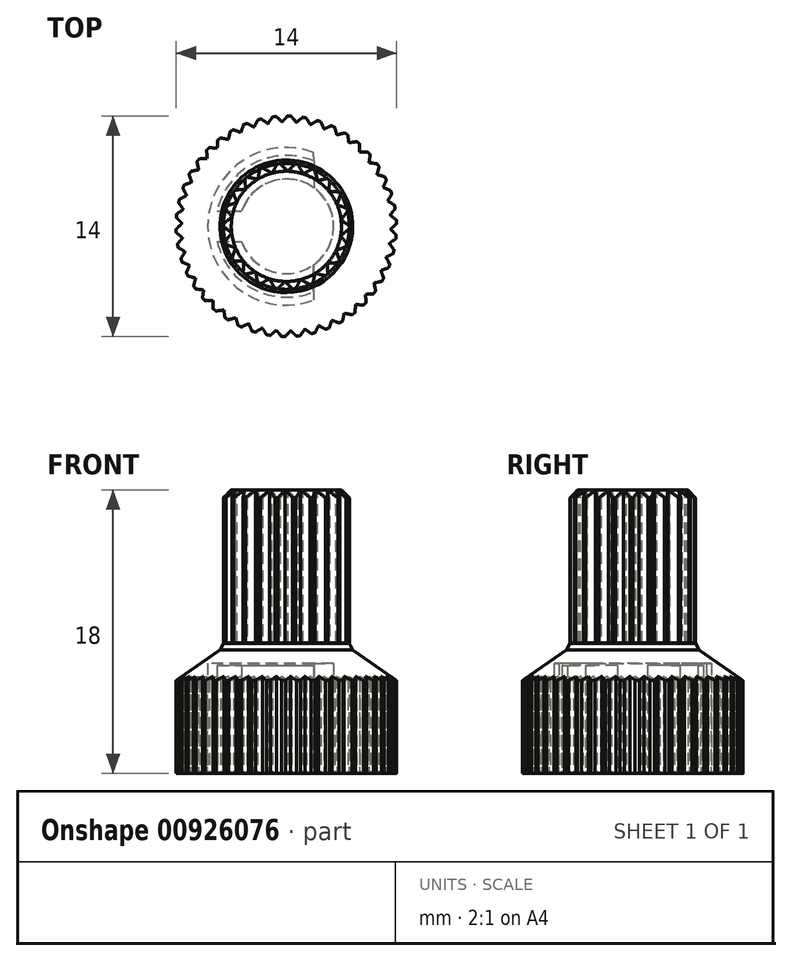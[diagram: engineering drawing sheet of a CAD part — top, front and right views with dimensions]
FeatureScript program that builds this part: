
annotation { "Feature Type Name" : "Feature", "Feature Type Description" : "" }
export const myFeature = defineFeature(function(context is Context, id is Id, definition is map)
    precondition{}
    {
        {
            var Q0;
            Q0=qCreatedBy(makeId("Top.planeOp"),FACE);
            var sketch = newSketch(context, id + "F0", { "sketchPlane" : qUnion([Q0])});
            skLineSegment(sketch, "E0", {"start": v(-2.85, 4.76) * mm, "end": v(-4.4, 4.76) * mm});
            skArc(sketch, "E1", {"start": v(-2.84, 2.85) * mm, "mid": v(3, 3.85) * mm, "end": v(-2.85, 4.76) * mm});
            skCircle(sketch, "E2", {"center": v(0, 3.83) * mm, "radius": 7 * mm});
            skArc(sketch, "E3", {"start": v(1.74, 8.52) * mm, "mid": v(-5, 3.83) * mm, "end": v(1.74, -0.86) * mm});
            skArc(sketch, "E4", {"start": v(1.76, 7.97) * mm, "mid": v(-2.08, 7.82) * mm, "end": v(-4.4, 4.76) * mm});
            skLineSegment(sketch, "E5", {"start": v(1.76, 7.97) * mm, "end": v(1.74, 8.52) * mm});
            skLineSegment(sketch, "E6", {"start": v(1.74, -0.32) * mm, "end": v(1.74, -0.86) * mm});
            skArc(sketch, "E7.trimOffspring", {"start": v(-4.4, 2.85) * mm, "mid": v(-2.07, -0.17) * mm, "end": v(1.74, -0.32) * mm});
            skLineSegment(sketch, "E8.trimOffspring", {"start": v(-4.4, 2.85) * mm, "end": v(-2.84, 2.85) * mm});
            skLineSegment(sketch, "E9", {"start": v(1.74, -0.32) * mm, "end": v(1.74, 1.38) * mm});
            skLineSegment(sketch, "E10", {"start": v(1.76, 7.97) * mm, "end": v(1.76, 6.26) * mm});
            skSolve(sketch);
        }
        {
            var Q0;
            Q0=makeQuery(id+"F0.imprint","IMPRINT",FACE,{"disambiguationData":[TD([[makeQuery(id+"F0.imprint","IMPRINT",EDGE,{"derivedFrom":sQuery(id+"F0.wireOp",EDGE,"E2")}),1.0]])]});
            var Q1;
            {var subQ0=sQuery(id+"F0.wireOp",EDGE,"E0");Q1=makeQuery(id+"F0.imprint","IMPRINT",FACE,{"disambiguationData":[TD([[makeQuery(id+"F0.imprint","IMPRINT",EDGE,{"derivedFrom":subQ0}),-1.0]])]});}
            var Q2;
            Q2=makeQuery(id+"F0.imprint","IMPRINT",FACE,{"disambiguationData":[TD([[makeQuery(id+"F0.imprint","IMPRINT",EDGE,{"derivedFrom":sQuery(id+"F0.wireOp",EDGE,"E7.trimOffspring")}),1.0]])]});
            var Q3;
            {var subQ1=sQuery(id+"F0.wireOp",EDGE,"E0");Q3=makeQuery(id+"F0.imprint","IMPRINT",FACE,{"disambiguationData":[TD([[makeQuery(id+"F0.imprint","IMPRINT",EDGE,{"derivedFrom":subQ1}),1.0]])]});}
            extrude(context, id + "F1", {"entities" : qUnion([Q0, Q1, Q2, Q3]), "depth" : 8 * mm});
        }
        {
            var Q0;
            Q0=makeQuery(id+"F0.imprint","IMPRINT",FACE,{"disambiguationData":[TD([[makeQuery(id+"F0.imprint","IMPRINT",EDGE,{"derivedFrom":sQuery(id+"F0.wireOp",EDGE,"E0")}),1.0]])]});
            extrude(context, id + "F2", {"entities" : qUnion([Q0]), "operationType" : NewBodyOperationType.REMOVE, "offsetDistance" : 25 * mm, "depth" : 7 * mm});
        }
        {
            var Q0;
            Q0=makeQuery(id+"F0.imprint","IMPRINT",FACE,{"disambiguationData":[TD([[makeQuery(id+"F0.imprint","IMPRINT",EDGE,{"derivedFrom":sQuery(id+"F0.wireOp",EDGE,"E7.trimOffspring")}),1.0]])]});
            var Q1;
            {var subQ0=sQuery(id+"F0.wireOp",EDGE,"E0");Q1=makeQuery(id+"F0.imprint","IMPRINT",FACE,{"disambiguationData":[TD([[makeQuery(id+"F0.imprint","IMPRINT",EDGE,{"derivedFrom":subQ0}),-1.0]])]});}
            extrude(context, id + "F3", {"entities" : qUnion([Q0, Q1]), "operationType" : NewBodyOperationType.REMOVE, "offsetDistance" : 25 * mm, "depth" : 7 * mm, "hasSecondDirection" : true, "secondDirectionOppositeDirection" : false, "secondDirectionDepth" : 6.85 * mm});
        }
        {
            var Q0;
            Q0=makeQuery(id+"F1.opExtrude","CAP_EDGE",EDGE,{"disambiguationData":[OSD([sQuery(id+"F0.wireOp",EDGE,"E2")])],"isStart":false});
            chamfer(context, id + "F4", {"entities" : qUnion([Q0]), "chamferType" : ChamferType.OFFSET_ANGLE, "width" : 3 * mm, "oppositeDirection" : false, "angle" : 35 * degree});
        }
        {
            var Q0;
            Q0=makeQuery(id+"F1.opExtrude","CAP_FACE",FACE,{"disambiguationData":[OSD([sQuery(id+"F0.wireOp",EDGE,"E2")])],"isStart":false});
            extrude(context, id + "F5", {"entities" : qUnion([Q0]), "operationType" : NewBodyOperationType.ADD, "depth" : 10 * mm});
        }
        {
            var Q0;
            Q0=makeQuery(id+"F5.opExtrude","CAP_EDGE",EDGE,{"disambiguationData":[OSD([sQuery(id+"F0.wireOp",EDGE,"E2")])],"isStart":false});
            var Q1;
            {var subQ0=sQuery(id+"F0.wireOp",EDGE,"E2");Q1=makeQuery(id+"F5.boolean.opBoolean","MERGE",EDGE,{"derivedFrom":[makeQuery(id+"F4.opChamfer","BLEND_EDGE",EDGE,{"blendedFrom":[makeQuery(id+"F1.opExtrude","CAP_EDGE",EDGE,{"disambiguationData":[OSD([subQ0])],"isStart":false}),makeQuery(id+"F1.opExtrude","CAP_FACE",FACE,{"disambiguationData":[OSD([subQ0])],"isStart":false})],"blendedInto":[makeQuery(id+"F1.opExtrude","CAP_FACE",FACE,{"disambiguationData":[OSD([subQ0])],"isStart":false})]}),makeQuery(id+"F5.opExtrude","CAP_EDGE",EDGE,{"disambiguationData":[OSD([subQ0])],"isStart":true})]});}
            chamfer(context, id + "F6", {"entities" : qUnion([Q0, Q1]), "width" : .5 * mm, "tangentPropagation" : true});
        }
        {
            var Q0;
            Q0=makeQuery(id+"F5.opExtrude","CAP_FACE",FACE,{"disambiguationData":[OSD([sQuery(id+"F0.wireOp",EDGE,"E2")])],"isStart":false});
            var sketch = newSketch(context, id + "F7", { "sketchPlane" : qUnion([Q0])});
            skLineSegment(sketch, "E11.bottom", {"start": v(-2.6, 8) * mm, "end": v(-1.62, 7.8) * mm});
            skLineSegment(sketch, "E11.top", {"start": v(-2.8, 7.02) * mm, "end": v(-1.82, 6.82) * mm});
            skLineSegment(sketch, "E11.left", {"start": v(-2.6, 8) * mm, "end": v(-2.8, 7.02) * mm});
            skLineSegment(sketch, "E11.right", {"start": v(-1.62, 7.8) * mm, "end": v(-1.82, 6.82) * mm});
            skPoint(sketch, "E12.firstSnap0", {"position": v(-1.72, 7.31) * mm});
            skLineSegment(sketch, "E13", {"start": v(-1.62, 7.8) * mm, "end": v(0, 7.47) * mm, "construction": true});
            skLineSegment(sketch, "E14", {"start": v(-2.8, 7.02) * mm, "end": v(-3.12, 5.4) * mm, "construction": true});
            skSolve(sketch);
        }
        {
            var Q0;
            Q0=makeQuery(id+"F7.imprint","IMPRINT",FACE,{"disambiguationData":[TD([[makeQuery(id+"F7.imprint","IMPRINT",EDGE,{"derivedFrom":sQuery(id+"F7.wireOp",EDGE,"E11.bottom")}),-1.0]])]});
            extrude(context, id + "F8", {"entities" : qUnion([Q0]), "oppositeDirection" : true, "depth" : 9.7 * mm});
        }
        {
            var Q0;
            Q0=makeQuery(id+"F8.opExtrude","SWEPT_BODY",BODY,{"disambiguationData":[OSD([sQuery(id+"F7.wireOp",EDGE,"E11.bottom"),sQuery(id+"F7.wireOp",EDGE,"E11.top"),sQuery(id+"F7.wireOp",EDGE,"E11.left"),sQuery(id+"F7.wireOp",EDGE,"E11.right")])]});
            var Q1;
            {var subQ0=sQuery(id+"F0.wireOp",EDGE,"E2");Q1=makeQuery(id+"F6.opChamfer","BLEND_EDGE",EDGE,{"blendedFrom":[makeQuery(id+"F5.opExtrude","CAP_EDGE",EDGE,{"disambiguationData":[OSD([subQ0])],"isStart":false}),makeQuery(id+"F5.opExtrude","CAP_FACE",FACE,{"disambiguationData":[OSD([subQ0])],"isStart":false})],"blendedInto":[makeQuery(id+"F5.opExtrude","CAP_FACE",FACE,{"disambiguationData":[OSD([subQ0])],"isStart":false})]});}
            circularPattern(context, id + "F9", {"operationType" : NewBodyOperationType.REMOVE, "entities" : qUnion([Q0]), "axis" : qUnion([Q1]), "angle" : 360 * degree, "instanceCount" : 22, "equalSpace" : true});
        }
        {
            var Q0;
            Q0=makeQuery(id+"F0.imprint","IMPRINT",FACE,{"disambiguationData":[TD([[makeQuery(id+"F0.imprint","IMPRINT",EDGE,{"derivedFrom":sQuery(id+"F0.wireOp",EDGE,"E2")}),1.0]])]});
            var sketch = newSketch(context, id + "F10", { "sketchPlane" : qUnion([Q0])});
            skLineSegment(sketch, "E15.bottom", {"start": v(-5.16, -1.4) * mm, "end": v(-4.66, -1.4) * mm});
            skLineSegment(sketch, "E15.top", {"start": v(-5.16, -0.9) * mm, "end": v(-4.66, -0.9) * mm});
            skLineSegment(sketch, "E15.left", {"start": v(-5.16, -1.4) * mm, "end": v(-5.16, -0.9) * mm});
            skLineSegment(sketch, "E15.right", {"start": v(-4.66, -1.4) * mm, "end": v(-4.66, -0.9) * mm});
            skSolve(sketch);
        }
        {
            var Q0;
            {var subQ2=sQuery(id+"F10.wireOp",EDGE,"E15.top");Q0=makeQuery(id+"F10.imprint","IMPRINT",FACE,{"disambiguationData":[TD([[makeQuery(id+"F10.imprint","IMPRINT",EDGE,{"derivedFrom":subQ2}),-1.0]])]});}
            var Q1;
            {var subQ0=sQuery(id+"F10.wireOp",EDGE,"E15.left");var subQ1=sQuery(id+"F10.wireOp",EDGE,"E15.bottom");var subQ2=makeQuery(id+"F10.imprint","INTERSECT",VERTEX,{"derivedFrom":[subQ1,subQ0]});Q1=makeQuery(id+"F10.imprint","IMPRINT",FACE,{"disambiguationData":[TD([[makeQuery(id+"F10.imprint","IMPRINT",EDGE,{"disambiguationData":[TD([[subQ2,-1.0]])],"derivedFrom":subQ1}),1.0]])]});}
            extrude(context, id + "F11", {"entities" : qUnion([Q0, Q1]), "depth" : 7 * mm});
        }
        {
            var Q0;
            Q0=makeQuery(id+"F11.opExtrude","SWEPT_BODY",BODY,{"disambiguationData":[OSD([sQuery(id+"F10.wireOp",EDGE,"E15.bottom"),sQuery(id+"F10.wireOp",EDGE,"E15.top"),sQuery(id+"F10.wireOp",EDGE,"E15.left"),sQuery(id+"F10.wireOp",EDGE,"E15.right")])]});
            var Q1;
            Q1=sQuery(id+"F0.wireOp",EDGE,"E2");
            circularPattern(context, id + "F12", {"operationType" : NewBodyOperationType.REMOVE, "entities" : qUnion([Q0]), "axis" : qUnion([Q1]), "angle" : 360 * degree, "instanceCount" : 46, "equalSpace" : true});
        }
    });
